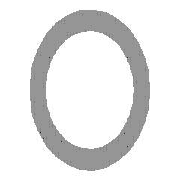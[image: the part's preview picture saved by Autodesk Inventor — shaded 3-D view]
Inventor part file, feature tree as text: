
AUTODESK INVENTOR PART (.ipt)
format: ipt  version: 2013 (Build 170138000, 138)  size: 108,032 bytes
history: native  units: mm (DEFAULTED — no unit token found)
features: other x4, sketch x3, plane x1
ambient origin geometry x8: Origin, YZ Plane, XZ Plane, XY Plane, X Axis, Y Axis, Z Axis, Center Point
bodies: Solid1 (feature_tree), Body (feature_tree)
feature tree (8):
  parser-record x1  (decoder bookkeeping rows leaked as tree rows — omitted from the tree; the rows remain in map.json)
  other  "Driven Length"
  other  "Start plane"
  other  "End plane"
  sketch  "Sketch"  dims[d2=1727.2mm d3=0.0mm d4=-0.0mm d5=1727.2mm d6=90.0deg d7=1727.2mm]
  sketch  "Sketch3"  dims[d0=42.164mm]
  plane  "Work Plane3"
  sketch  "Sketch4"  dims[d1=3.556mm]
